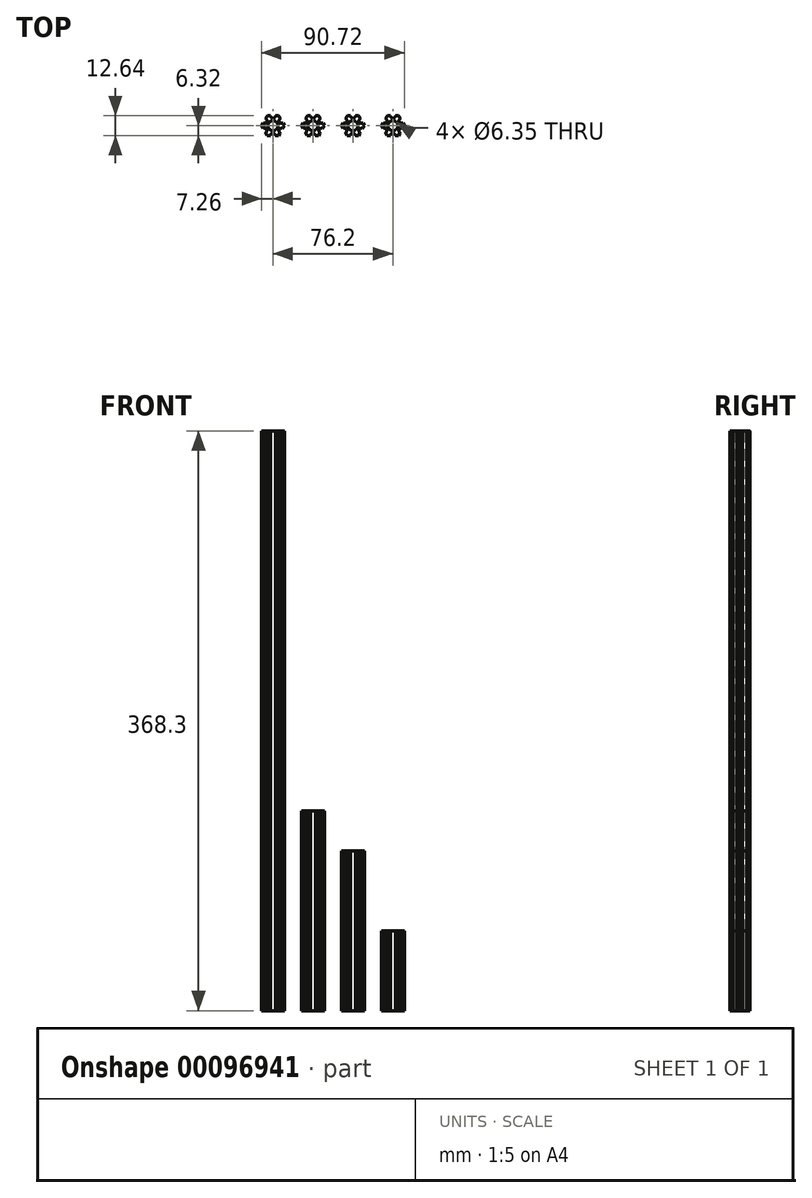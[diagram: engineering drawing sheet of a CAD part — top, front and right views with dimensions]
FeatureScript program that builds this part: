
annotation { "Feature Type Name" : "Feature", "Feature Type Description" : "" }
export const myFeature = defineFeature(function(context is Context, id is Id, definition is map)
    precondition{}
    {
        {
            var Q0;
            Q0=qCreatedBy(makeId("Top.planeOp"),FACE);
            var sketch = newSketch(context, id + "F0", { "sketchPlane" : qUnion([Q0])});
            skLineSegment(sketch, "E0.0", {"start": v(3.69, 6.25) * mm, "end": v(4.7, 4.48) * mm});
            skLineSegment(sketch, "E0.1", {"start": v(7.26, -0.07) * mm, "end": v(6.22, -1.82) * mm});
            skLineSegment(sketch, "E0.2", {"start": v(3.57, -6.32) * mm, "end": v(1.53, -6.3) * mm});
            skLineSegment(sketch, "E0.3", {"start": v(-3.69, -6.25) * mm, "end": v(-4.7, -4.48) * mm});
            skLineSegment(sketch, "E0.4", {"start": v(-7.26, 0.07) * mm, "end": v(-6.22, 1.82) * mm});
            skLineSegment(sketch, "E0.5", {"start": v(-3.57, 6.32) * mm, "end": v(-1.59, 6.3) * mm});
            skPoint(sketch, "E0.0.midPoint", {"position": v(5.47, 3.1) * mm});
            skCircle(sketch, "E1", {"center": v(0, 0) * mm, "radius": 3.18 * mm});
            skArc(sketch, "E2", {"start": v(-6.22, 1.82) * mm, "mid": v(-4.05, 2.39) * mm, "end": v(-4.6, 4.56) * mm});
            skLineSegment(sketch, "E3.trimOffspring", {"start": v(-4.6, 4.56) * mm, "end": v(-3.57, 6.32) * mm});
            skArc(sketch, "E4", {"start": v(-1.59, 6.3) * mm, "mid": v(-0.01, 4.7) * mm, "end": v(1.59, 6.27) * mm});
            skLineSegment(sketch, "E5.trimOffspring", {"start": v(1.59, 6.27) * mm, "end": v(3.69, 6.25) * mm});
            skArc(sketch, "E6", {"start": v(4.7, 4.48) * mm, "mid": v(4.1, 2.31) * mm, "end": v(6.25, 1.71) * mm});
            skArc(sketch, "E7", {"start": v(6.22, -1.82) * mm, "mid": v(4.05, -2.39) * mm, "end": v(4.6, -4.56) * mm});
            skArc(sketch, "E8", {"start": v(1.53, -6.3) * mm, "mid": v(-0.04, -4.7) * mm, "end": v(-1.64, -6.27) * mm});
            skArc(sketch, "E9", {"start": v(-4.7, -4.48) * mm, "mid": v(-4.1, -2.31) * mm, "end": v(-6.25, -1.71) * mm});
            skLineSegment(sketch, "E10.trimOffspring", {"start": v(-6.25, -1.71) * mm, "end": v(-7.26, 0.07) * mm});
            skLineSegment(sketch, "E11.trimOffspring", {"start": v(-1.64, -6.27) * mm, "end": v(-3.69, -6.25) * mm});
            skLineSegment(sketch, "E12.trimOffspring", {"start": v(4.6, -4.56) * mm, "end": v(3.57, -6.32) * mm});
            skLineSegment(sketch, "E13.trimOffspring", {"start": v(6.25, 1.71) * mm, "end": v(7.26, -0.07) * mm});
            skSolve(sketch);
        }
        {
            var Q0;
            Q0=makeQuery(id+"F0.imprint","IMPRINT",FACE,{"disambiguationData":[TD([[makeQuery(id+"F0.imprint","IMPRINT",EDGE,{"derivedFrom":sQuery(id+"F0.wireOp",EDGE,"E0.0")}),-1.0]])]});
            extrude(context, id + "F1", {"entities" : qUnion([Q0]), "depth" : 368.3 * mm});
        }
        {
            var Q0;
            Q0=makeQuery(id+"F1.opExtrude","SWEPT_BODY",BODY,{"disambiguationData":[OSD([sQuery(id+"F0.wireOp",EDGE,"E0.0"),sQuery(id+"F0.wireOp",EDGE,"E0.1"),sQuery(id+"F0.wireOp",EDGE,"E0.2"),sQuery(id+"F0.wireOp",EDGE,"E0.3"),sQuery(id+"F0.wireOp",EDGE,"E0.4"),sQuery(id+"F0.wireOp",EDGE,"E0.5"),sQuery(id+"F0.wireOp",EDGE,"E1"),sQuery(id+"F0.wireOp",EDGE,"E2"),sQuery(id+"F0.wireOp",EDGE,"E3.trimOffspring"),sQuery(id+"F0.wireOp",EDGE,"E4"),sQuery(id+"F0.wireOp",EDGE,"E5.trimOffspring"),sQuery(id+"F0.wireOp",EDGE,"E6"),sQuery(id+"F0.wireOp",EDGE,"E7"),sQuery(id+"F0.wireOp",EDGE,"E8"),sQuery(id+"F0.wireOp",EDGE,"E9"),sQuery(id+"F0.wireOp",EDGE,"E10.trimOffspring"),sQuery(id+"F0.wireOp",EDGE,"E11.trimOffspring"),sQuery(id+"F0.wireOp",EDGE,"E12.trimOffspring"),sQuery(id+"F0.wireOp",EDGE,"E13.trimOffspring")])]});
            transform(context, id + "F2", {"entities" : qUnion([Q0]), "transformType" : TransformType.TRANSLATION_3D, "dx" : 0 * mm, "dy" : 0 * mm, "dz" : 0 * mm, "makeCopy" : true});
        }
        {
            var Q0;
            Q0=makeQuery(id+"F2.opPattern","COPY",BODY,{"derivedFrom":makeQuery(id+"F1.opExtrude","SWEPT_BODY",BODY,{"disambiguationData":[OSD([sQuery(id+"F0.wireOp",EDGE,"E0.0"),sQuery(id+"F0.wireOp",EDGE,"E0.1"),sQuery(id+"F0.wireOp",EDGE,"E0.2"),sQuery(id+"F0.wireOp",EDGE,"E0.3"),sQuery(id+"F0.wireOp",EDGE,"E0.4"),sQuery(id+"F0.wireOp",EDGE,"E0.5"),sQuery(id+"F0.wireOp",EDGE,"E1"),sQuery(id+"F0.wireOp",EDGE,"E2"),sQuery(id+"F0.wireOp",EDGE,"E3.trimOffspring"),sQuery(id+"F0.wireOp",EDGE,"E4"),sQuery(id+"F0.wireOp",EDGE,"E5.trimOffspring"),sQuery(id+"F0.wireOp",EDGE,"E6"),sQuery(id+"F0.wireOp",EDGE,"E7"),sQuery(id+"F0.wireOp",EDGE,"E8"),sQuery(id+"F0.wireOp",EDGE,"E9"),sQuery(id+"F0.wireOp",EDGE,"E10.trimOffspring"),sQuery(id+"F0.wireOp",EDGE,"E11.trimOffspring"),sQuery(id+"F0.wireOp",EDGE,"E12.trimOffspring"),sQuery(id+"F0.wireOp",EDGE,"E13.trimOffspring")])]}),"instanceName":"1"});
            deleteBodies(context, id + "F3", {"entities" : qUnion([Q0])});
        }
        {
            var Q0;
            Q0=makeQuery(id+"F1.opExtrude","SWEPT_BODY",BODY,{"disambiguationData":[OSD([sQuery(id+"F0.wireOp",EDGE,"E0.0"),sQuery(id+"F0.wireOp",EDGE,"E0.1"),sQuery(id+"F0.wireOp",EDGE,"E0.2"),sQuery(id+"F0.wireOp",EDGE,"E0.3"),sQuery(id+"F0.wireOp",EDGE,"E0.4"),sQuery(id+"F0.wireOp",EDGE,"E0.5"),sQuery(id+"F0.wireOp",EDGE,"E1"),sQuery(id+"F0.wireOp",EDGE,"E2"),sQuery(id+"F0.wireOp",EDGE,"E3.trimOffspring"),sQuery(id+"F0.wireOp",EDGE,"E4"),sQuery(id+"F0.wireOp",EDGE,"E5.trimOffspring"),sQuery(id+"F0.wireOp",EDGE,"E6"),sQuery(id+"F0.wireOp",EDGE,"E7"),sQuery(id+"F0.wireOp",EDGE,"E8"),sQuery(id+"F0.wireOp",EDGE,"E9"),sQuery(id+"F0.wireOp",EDGE,"E10.trimOffspring"),sQuery(id+"F0.wireOp",EDGE,"E11.trimOffspring"),sQuery(id+"F0.wireOp",EDGE,"E12.trimOffspring"),sQuery(id+"F0.wireOp",EDGE,"E13.trimOffspring")])]});
            transform(context, id + "F4", {"entities" : qUnion([Q0]), "transformType" : TransformType.TRANSLATION_3D, "dx" : 25.4 * mm, "dy" : 0 * mm, "dz" : 0 * mm, "makeCopy" : true});
        }
        {
            var Q0;
            Q0=makeQuery(id+"F4.opPattern","COPY",FACE,{"derivedFrom":makeQuery(id+"F1.opExtrude","CAP_FACE",FACE,{"disambiguationData":[OSD([sQuery(id+"F0.wireOp",EDGE,"E0.0"),sQuery(id+"F0.wireOp",EDGE,"E0.1"),sQuery(id+"F0.wireOp",EDGE,"E0.2"),sQuery(id+"F0.wireOp",EDGE,"E0.3"),sQuery(id+"F0.wireOp",EDGE,"E0.4"),sQuery(id+"F0.wireOp",EDGE,"E0.5"),sQuery(id+"F0.wireOp",EDGE,"E1"),sQuery(id+"F0.wireOp",EDGE,"E2"),sQuery(id+"F0.wireOp",EDGE,"E3.trimOffspring"),sQuery(id+"F0.wireOp",EDGE,"E4"),sQuery(id+"F0.wireOp",EDGE,"E5.trimOffspring"),sQuery(id+"F0.wireOp",EDGE,"E6"),sQuery(id+"F0.wireOp",EDGE,"E7"),sQuery(id+"F0.wireOp",EDGE,"E8"),sQuery(id+"F0.wireOp",EDGE,"E9"),sQuery(id+"F0.wireOp",EDGE,"E10.trimOffspring"),sQuery(id+"F0.wireOp",EDGE,"E11.trimOffspring"),sQuery(id+"F0.wireOp",EDGE,"E12.trimOffspring"),sQuery(id+"F0.wireOp",EDGE,"E13.trimOffspring")])],"isStart":false}),"instanceName":"1"});
            extrude(context, id + "F5", {"entities" : qUnion([Q0]), "operationType" : NewBodyOperationType.REMOVE, "oppositeDirection" : true, "depth" : 241.3 * mm});
        }
        {
            var Q0;
            Q0=makeQuery(id+"F1.opExtrude","SWEPT_BODY",BODY,{"disambiguationData":[OSD([sQuery(id+"F0.wireOp",EDGE,"E0.0"),sQuery(id+"F0.wireOp",EDGE,"E0.1"),sQuery(id+"F0.wireOp",EDGE,"E0.2"),sQuery(id+"F0.wireOp",EDGE,"E0.3"),sQuery(id+"F0.wireOp",EDGE,"E0.4"),sQuery(id+"F0.wireOp",EDGE,"E0.5"),sQuery(id+"F0.wireOp",EDGE,"E1"),sQuery(id+"F0.wireOp",EDGE,"E2"),sQuery(id+"F0.wireOp",EDGE,"E3.trimOffspring"),sQuery(id+"F0.wireOp",EDGE,"E4"),sQuery(id+"F0.wireOp",EDGE,"E5.trimOffspring"),sQuery(id+"F0.wireOp",EDGE,"E6"),sQuery(id+"F0.wireOp",EDGE,"E7"),sQuery(id+"F0.wireOp",EDGE,"E8"),sQuery(id+"F0.wireOp",EDGE,"E9"),sQuery(id+"F0.wireOp",EDGE,"E10.trimOffspring"),sQuery(id+"F0.wireOp",EDGE,"E11.trimOffspring"),sQuery(id+"F0.wireOp",EDGE,"E12.trimOffspring"),sQuery(id+"F0.wireOp",EDGE,"E13.trimOffspring")])]});
            transform(context, id + "F6", {"entities" : qUnion([Q0]), "transformType" : TransformType.TRANSLATION_3D, "dx" : 50.8 * mm, "dy" : 0 * mm, "dz" : 0 * mm, "makeCopy" : true});
        }
        {
            var Q0;
            Q0=makeQuery(id+"F6.opPattern","COPY",FACE,{"derivedFrom":makeQuery(id+"F1.opExtrude","CAP_FACE",FACE,{"disambiguationData":[OSD([sQuery(id+"F0.wireOp",EDGE,"E0.0"),sQuery(id+"F0.wireOp",EDGE,"E0.1"),sQuery(id+"F0.wireOp",EDGE,"E0.2"),sQuery(id+"F0.wireOp",EDGE,"E0.3"),sQuery(id+"F0.wireOp",EDGE,"E0.4"),sQuery(id+"F0.wireOp",EDGE,"E0.5"),sQuery(id+"F0.wireOp",EDGE,"E1"),sQuery(id+"F0.wireOp",EDGE,"E2"),sQuery(id+"F0.wireOp",EDGE,"E3.trimOffspring"),sQuery(id+"F0.wireOp",EDGE,"E4"),sQuery(id+"F0.wireOp",EDGE,"E5.trimOffspring"),sQuery(id+"F0.wireOp",EDGE,"E6"),sQuery(id+"F0.wireOp",EDGE,"E7"),sQuery(id+"F0.wireOp",EDGE,"E8"),sQuery(id+"F0.wireOp",EDGE,"E9"),sQuery(id+"F0.wireOp",EDGE,"E10.trimOffspring"),sQuery(id+"F0.wireOp",EDGE,"E11.trimOffspring"),sQuery(id+"F0.wireOp",EDGE,"E12.trimOffspring"),sQuery(id+"F0.wireOp",EDGE,"E13.trimOffspring")])],"isStart":false}),"instanceName":"1"});
            extrude(context, id + "F7", {"entities" : qUnion([Q0]), "operationType" : NewBodyOperationType.REMOVE, "oppositeDirection" : true, "depth" : 266.7 * mm});
        }
        {
            var Q0;
            Q0=makeQuery(id+"F6.opPattern","COPY",BODY,{"derivedFrom":makeQuery(id+"F1.opExtrude","SWEPT_BODY",BODY,{"disambiguationData":[OSD([sQuery(id+"F0.wireOp",EDGE,"E0.0"),sQuery(id+"F0.wireOp",EDGE,"E0.1"),sQuery(id+"F0.wireOp",EDGE,"E0.2"),sQuery(id+"F0.wireOp",EDGE,"E0.3"),sQuery(id+"F0.wireOp",EDGE,"E0.4"),sQuery(id+"F0.wireOp",EDGE,"E0.5"),sQuery(id+"F0.wireOp",EDGE,"E1"),sQuery(id+"F0.wireOp",EDGE,"E2"),sQuery(id+"F0.wireOp",EDGE,"E3.trimOffspring"),sQuery(id+"F0.wireOp",EDGE,"E4"),sQuery(id+"F0.wireOp",EDGE,"E5.trimOffspring"),sQuery(id+"F0.wireOp",EDGE,"E6"),sQuery(id+"F0.wireOp",EDGE,"E7"),sQuery(id+"F0.wireOp",EDGE,"E8"),sQuery(id+"F0.wireOp",EDGE,"E9"),sQuery(id+"F0.wireOp",EDGE,"E10.trimOffspring"),sQuery(id+"F0.wireOp",EDGE,"E11.trimOffspring"),sQuery(id+"F0.wireOp",EDGE,"E12.trimOffspring"),sQuery(id+"F0.wireOp",EDGE,"E13.trimOffspring")])]}),"instanceName":"1"});
            transform(context, id + "F8", {"entities" : qUnion([Q0]), "transformType" : TransformType.TRANSLATION_3D, "dx" : 25.4 * mm, "dy" : 0 * mm, "dz" : 0 * mm, "makeCopy" : true});
        }
        {
            var Q0;
            Q0=makeQuery(id+"F8.opPattern","COPY",FACE,{"derivedFrom":makeQuery(id+"F7.boolean.opBoolean","COPY",FACE,{"derivedFrom":makeQuery(id+"F7.opExtrude","CAP_FACE",FACE,{"disambiguationData":[OSD([sQuery(id+"F0.wireOp",EDGE,"E0.0"),sQuery(id+"F0.wireOp",EDGE,"E0.1"),sQuery(id+"F0.wireOp",EDGE,"E0.2"),sQuery(id+"F0.wireOp",EDGE,"E0.3"),sQuery(id+"F0.wireOp",EDGE,"E0.4"),sQuery(id+"F0.wireOp",EDGE,"E0.5"),sQuery(id+"F0.wireOp",EDGE,"E1"),sQuery(id+"F0.wireOp",EDGE,"E2"),sQuery(id+"F0.wireOp",EDGE,"E3.trimOffspring"),sQuery(id+"F0.wireOp",EDGE,"E4"),sQuery(id+"F0.wireOp",EDGE,"E5.trimOffspring"),sQuery(id+"F0.wireOp",EDGE,"E6"),sQuery(id+"F0.wireOp",EDGE,"E7"),sQuery(id+"F0.wireOp",EDGE,"E8"),sQuery(id+"F0.wireOp",EDGE,"E9"),sQuery(id+"F0.wireOp",EDGE,"E10.trimOffspring"),sQuery(id+"F0.wireOp",EDGE,"E11.trimOffspring"),sQuery(id+"F0.wireOp",EDGE,"E12.trimOffspring"),sQuery(id+"F0.wireOp",EDGE,"E13.trimOffspring")])],"isStart":false})}),"instanceName":"1"});
            extrude(context, id + "F9", {"entities" : qUnion([Q0]), "operationType" : NewBodyOperationType.REMOVE, "oppositeDirection" : true, "depth" : 50.8 * mm});
        }
    });
